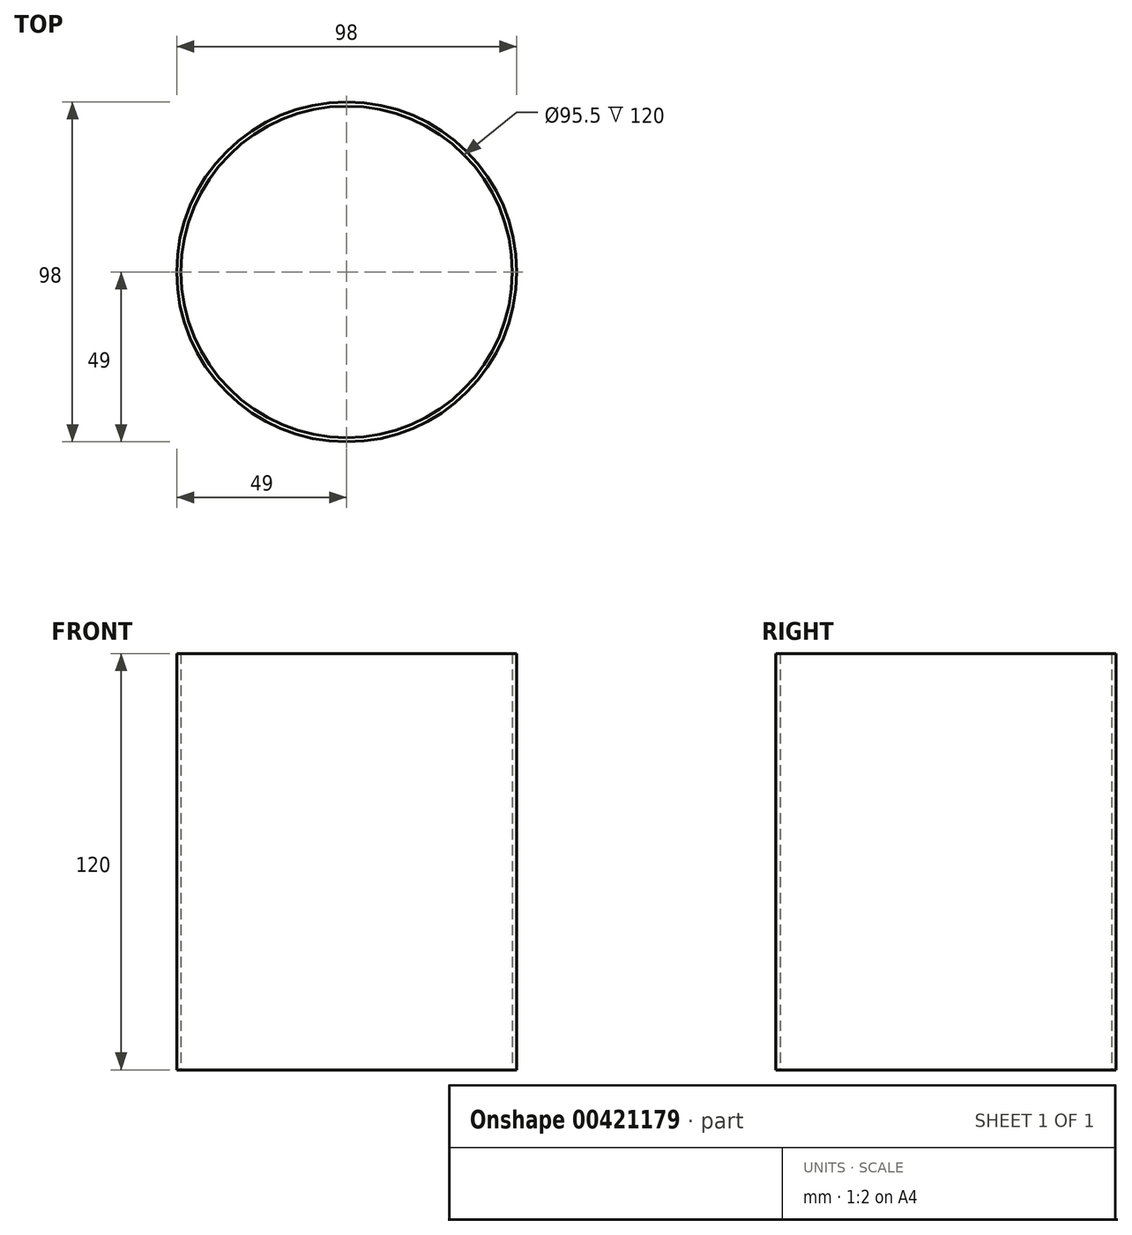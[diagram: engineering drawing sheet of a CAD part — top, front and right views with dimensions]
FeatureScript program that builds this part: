
annotation { "Feature Type Name" : "Feature", "Feature Type Description" : "" }
export const myFeature = defineFeature(function(context is Context, id is Id, definition is map)
    precondition{}
    {
        {
            var Q0;
            Q0=qCreatedBy(makeId("Top.planeOp"),FACE);
            var sketch = newSketch(context, id + "F0", { "sketchPlane" : qUnion([Q0])});
            skCircle(sketch, "E0", {"center": v(0, 0) * mm, "radius": 47.75 * mm});
            skCircle(sketch, "E1", {"center": v(0, 0) * mm, "radius": 49 * mm});
            skSolve(sketch);
        }
        {
            var Q0;
            Q0 = qSketchRegion(id + "F0", true);
            extrude(context, id + "F1", {"entities" : qUnion([Q0]), "depth" : 120 * mm});
        }
    });
